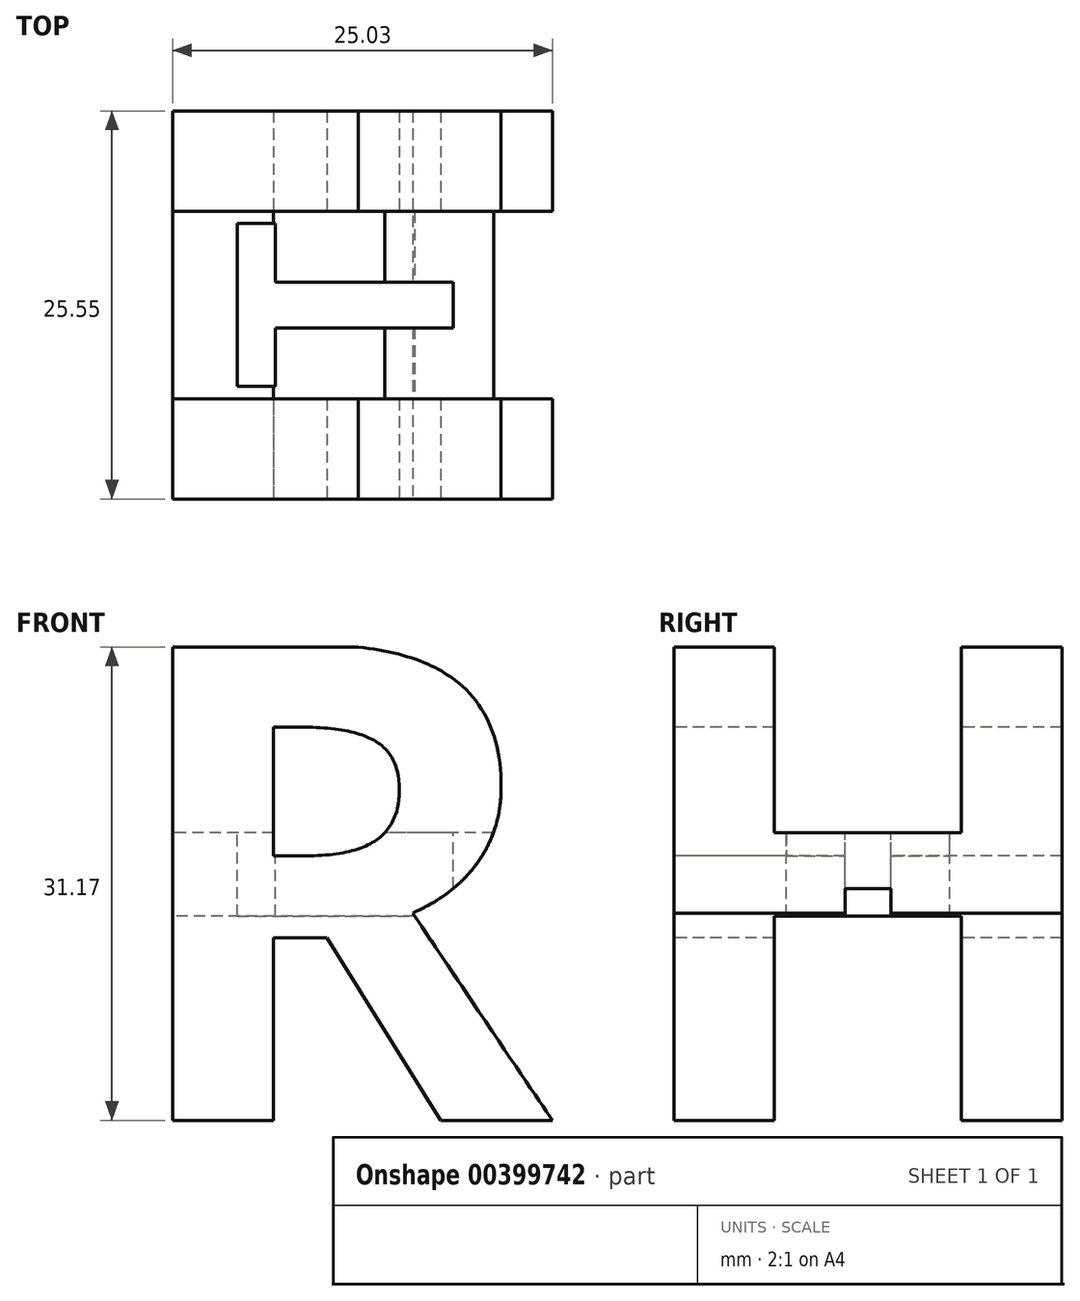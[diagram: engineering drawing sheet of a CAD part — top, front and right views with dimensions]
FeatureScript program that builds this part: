
annotation { "Feature Type Name" : "Feature", "Feature Type Description" : "" }
export const myFeature = defineFeature(function(context is Context, id is Id, definition is map)
    precondition{}
    {
        {
            var Q0;
            Q0=qCreatedBy(makeId("Front.planeOp"),FACE);
            var sketch = newSketch(context, id + "F0", { "sketchPlane" : qUnion([Q0])});
            skLineSegment(sketch, "E0.bottom", {"start": v(0, 0) * mm, "end": v(31.75, 0) * mm});
            skLineSegment(sketch, "E0.top", {"start": v(0, 31.75) * mm, "end": v(31.75, 31.75) * mm});
            skLineSegment(sketch, "E0.left", {"start": v(0, 0) * mm, "end": v(0, 31.75) * mm});
            skLineSegment(sketch, "E0.right", {"start": v(31.75, 0) * mm, "end": v(31.75, 31.75) * mm});
            skSolve(sketch);
        }
        {
            var Q0;
            Q0 = qSketchRegion(id + "F0", true);
            extrude(context, id + "F1", {"entities" : qUnion([Q0]), "depth" : 31.75 * mm});
        }
        {
            var Q0;
            Q0=makeQuery(id+"F1.opExtrude","CAP_FACE",FACE,{"disambiguationData":[OSD([sQuery(id+"F0.wireOp",EDGE,"E0.bottom"),sQuery(id+"F0.wireOp",EDGE,"E0.top"),sQuery(id+"F0.wireOp",EDGE,"E0.left"),sQuery(id+"F0.wireOp",EDGE,"E0.right")])],"isStart":false});
            var sketch = newSketch(context, id + "F2", { "sketchPlane" : qUnion([Q0])});
            skText(sketch, "E1", { "text": "R", "fontName": "OpenSans-Bold.ttf"});
            const initialGuessF2  = {"E1": [-2e-05, 0, 1, 0, 0.0316]};
            skSetInitialGuess(sketch, initialGuessF2);
            skSolve(sketch);
        }
        {
            var Q0;
            {var subQ2=sQuery(id+"F2.wireOp",EDGE,"E1.sketch_text.stroke-9");Q0=makeQuery(id+"F2.imprint","IMPRINT",FACE,{"disambiguationData":[TD([[makeQuery(id+"F2.imprint","IMPRINT",EDGE,{"derivedFrom":subQ2}),1.0]])]});}
            var Q1;
            {var subQ0=sQuery(id+"F2.wireOp",EDGE,"E1.sketch_text.stroke-7");Q1=makeQuery(id+"F2.imprint","IMPRINT",FACE,{"disambiguationData":[TD([[makeQuery(id+"F2.imprint","IMPRINT",EDGE,{"derivedFrom":subQ0}),1.0]])]});}
            var Q2;
            Q2=makeQuery(id+"F2.imprint","IMPRINT",FACE,{"disambiguationData":[TD([[makeQuery(id+"F2.imprint","IMPRINT",EDGE,{"derivedFrom":sQuery(id+"F2.wireOp",EDGE,"E1.sketch_text.stroke-0")}),1.0]])]});
            extrude(context, id + "F3", {"entities" : qUnion([Q0, Q1, Q2]), "operationType" : NewBodyOperationType.REMOVE, "endBound" : BoundingType.THROUGH_ALL, "oppositeDirection" : true, "depth" : 25.4 * mm});
        }
        {
            var Q0;
            Q0=makeQuery(id+"F3.boolean.opBoolean","COPY",FACE,{"derivedFrom":makeQuery(id+"F3.opExtrude","SWEPT_FACE",FACE,{"disambiguationData":[OSD([sQuery(id+"F2.wireOp",EDGE,"E1.sketch_text.stroke-9")])]})});
            var sketch = newSketch(context, id + "F4", { "sketchPlane" : qUnion([Q0])});
            skText(sketch, "E2", { "text": "H", "fontName": "OpenSans-Bold.ttf"});
            const initialGuessF4  = {"E2": [-0.00086, 0, 1, 0, 0.03144]};
            skSetInitialGuess(sketch, initialGuessF4);
            skSolve(sketch);
        }
        {
            var Q0;
            {var subQ5=sQuery(id+"F4.wireOp",EDGE,"E2.sketch_text.stroke-5");Q0=makeQuery(id+"F4.imprint","IMPRINT",FACE,{"disambiguationData":[TD([[makeQuery(id+"F4.imprint","IMPRINT",EDGE,{"derivedFrom":subQ5}),1.0]])]});}
            var Q1;
            {var subQ0=sQuery(id+"F4.wireOp",EDGE,"E2.sketch_text.stroke-1");Q1=makeQuery(id+"F4.imprint","IMPRINT",FACE,{"disambiguationData":[TD([[makeQuery(id+"F4.imprint","IMPRINT",EDGE,{"derivedFrom":subQ0}),1.0]])]});}
            extrude(context, id + "F5", {"entities" : qUnion([Q0, Q1]), "operationType" : NewBodyOperationType.REMOVE, "endBound" : BoundingType.THROUGH_ALL, "oppositeDirection" : true, "depth" : 25.4 * mm});
        }
        {
            var Q0;
            Q0=makeQuery(id+"F5.boolean.opBoolean","COPY",FACE,{"derivedFrom":makeQuery(id+"F5.opExtrude","SWEPT_FACE",FACE,{"disambiguationData":[OSD([sQuery(id+"F4.wireOp",EDGE,"E2.sketch_text.stroke-10")])]})});
            var sketch = newSketch(context, id + "F6", { "sketchPlane" : qUnion([Q0])});
            skText(sketch, "E3", { "text": "T", "fontName": "OpenSans-Bold.ttf"});
            const initialGuessF6  = {"E3": [0.0224, -0.0216, 0, 1, 0.01434]};
            skSetInitialGuess(sketch, initialGuessF6);
            skSolve(sketch);
        }
        {
            var Q0;
            Q0=makeQuery(id+"F6.imprint","IMPRINT",FACE,{"disambiguationData":[TD([[makeQuery(id+"F6.imprint","IMPRINT",EDGE,{"derivedFrom":sQuery(id+"F6.wireOp",EDGE,"E3.sketch_text.stroke-0")}),-1.0]])]});
            extrude(context, id + "F7", {"entities" : qUnion([Q0]), "operationType" : NewBodyOperationType.REMOVE, "endBound" : BoundingType.THROUGH_ALL, "oppositeDirection" : true, "depth" : 25.4 * mm});
        }
    });
